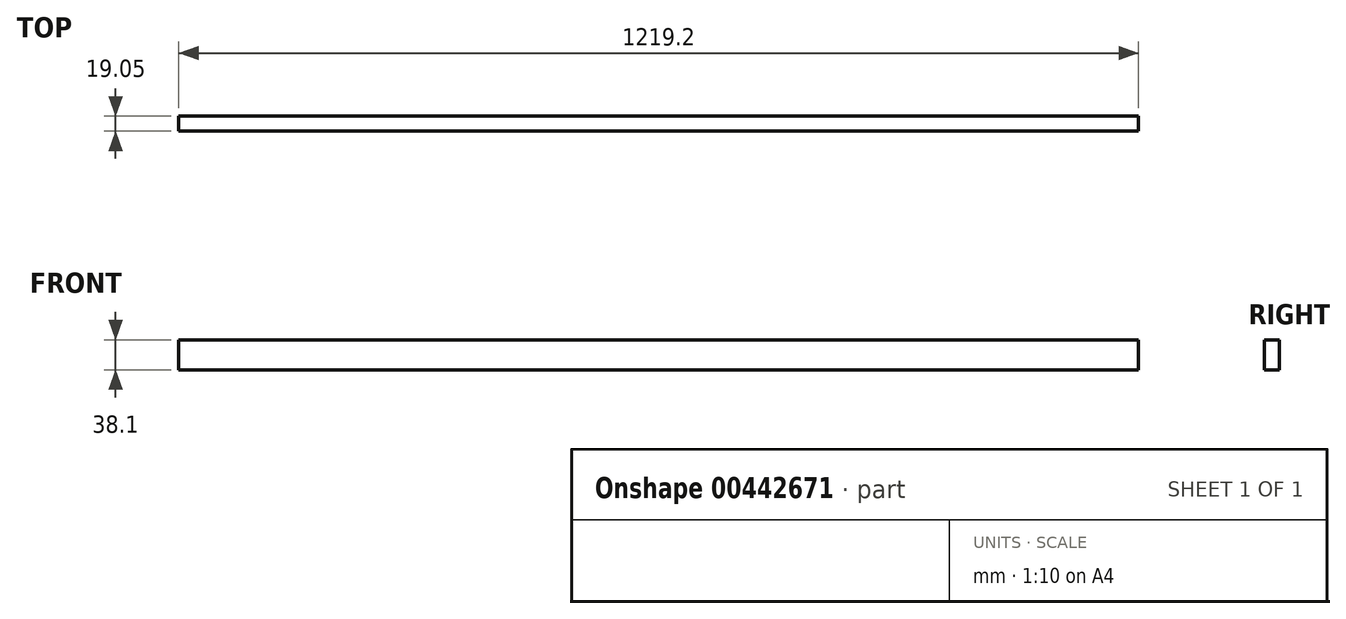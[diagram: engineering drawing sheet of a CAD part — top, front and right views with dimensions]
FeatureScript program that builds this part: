
annotation { "Feature Type Name" : "Feature", "Feature Type Description" : "" }
export const myFeature = defineFeature(function(context is Context, id is Id, definition is map)
    precondition{}
    {
        {
            var Q0;
            Q0=qCreatedBy(makeId("Front.planeOp"),FACE);
            var sketch = newSketch(context, id + "F0", { "sketchPlane" : qUnion([Q0])});
            skLineSegment(sketch, "E0.bottom", {"start": v(0, 0) * mm, "end": v(1219.2, 0) * mm});
            skLineSegment(sketch, "E0.top", {"start": v(0, 38.1) * mm, "end": v(1219.2, 38.1) * mm});
            skLineSegment(sketch, "E0.left", {"start": v(0, 0) * mm, "end": v(0, 38.1) * mm});
            skLineSegment(sketch, "E0.right", {"start": v(1219.2, 0) * mm, "end": v(1219.2, 38.1) * mm});
            skSolve(sketch);
        }
        {
            var Q0;
            Q0 = qSketchRegion(id + "F0", true);
            extrude(context, id + "F1", {"entities" : qUnion([Q0]), "depth" : 19.05 * mm});
        }
    });
